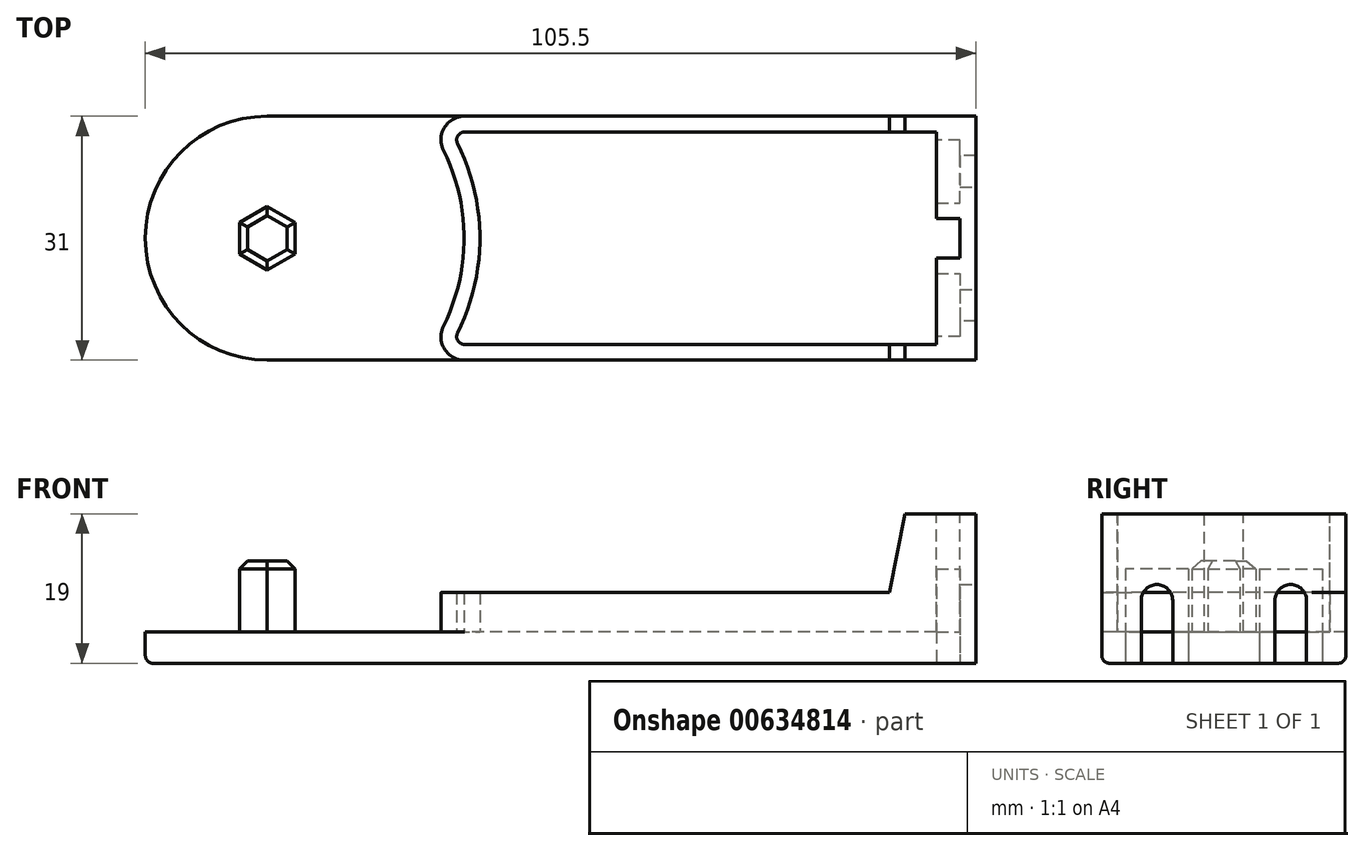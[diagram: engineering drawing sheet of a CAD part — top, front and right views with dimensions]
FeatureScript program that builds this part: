
annotation { "Feature Type Name" : "Feature", "Feature Type Description" : "" }
export const myFeature = defineFeature(function(context is Context, id is Id, definition is map)
    precondition{}
    {
        {
            var Q0;
            Q0=qCreatedBy(makeId("Top.planeOp"),FACE);
            var sketch = newSketch(context, id + "F0", { "sketchPlane" : qUnion([Q0])});
            skCircle(sketch, "E0", {"center": v(0, 0) * mm, "radius": 15.5 * mm});
            skLineSegment(sketch, "E1.bottom", {"start": v(0, 15.5) * mm, "end": v(90, 15.5) * mm});
            skLineSegment(sketch, "E1.top", {"start": v(0, -15.5) * mm, "end": v(90, -15.5) * mm});
            skLineSegment(sketch, "E1.left", {"start": v(0, 15.5) * mm, "end": v(0, -15.5) * mm});
            skLineSegment(sketch, "E1.right", {"start": v(90, 15.5) * mm, "end": v(90, -15.5) * mm});
            skSolve(sketch);
        }
        {
            var Q0;
            Q0=qSketchRegion(id+"F0",true);
            extrude(context, id + "F1", {"entities" : qUnion([Q0]), "depth" : 4 * mm, "offsetDistance" : 25 * mm});
        }
        {
            var Q0;
            Q0=makeQuery(id+"F1.opExtrude","CAP_FACE",FACE,{"disambiguationData":[OSD([sQuery(id+"F0.wireOp",EDGE,"E0"),sQuery(id+"F0.wireOp",EDGE,"E1.bottom"),sQuery(id+"F0.wireOp",EDGE,"E1.top"),sQuery(id+"F0.wireOp",EDGE,"E1.right")])],"isStart":false});
            var sketch = newSketch(context, id + "F2", { "sketchPlane" : qUnion([Q0])});
            skLineSegment(sketch, "E2", {"start": v(0, 0) * mm, "end": v(-3.5, 0) * mm});
            skCircle(sketch, "E3.cCircle", {"center": v(0, 0) * mm, "radius": 3.5 * mm, "construction": true});
            skLineSegment(sketch, "E3.0", {"start": v(-3.5, -2.02) * mm, "end": v(-3.5, 2.02) * mm});
            skLineSegment(sketch, "E3.1", {"start": v(-3.5, 2.02) * mm, "end": v(0, 4.04) * mm});
            skLineSegment(sketch, "E3.2", {"start": v(0, 4.04) * mm, "end": v(3.5, 2.02) * mm});
            skLineSegment(sketch, "E3.3", {"start": v(3.5, 2.02) * mm, "end": v(3.5, -2.02) * mm});
            skLineSegment(sketch, "E3.4", {"start": v(3.5, -2.02) * mm, "end": v(0, -4.04) * mm});
            skLineSegment(sketch, "E3.5", {"start": v(0, -4.04) * mm, "end": v(-3.5, -2.02) * mm});
            skPoint(sketch, "E3.0.midPoint", {"position": v(-3.5, 0) * mm});
            skSolve(sketch);
        }
        {
            var Q0;
            Q0=qSketchRegion(id+"F2",true);
            extrude(context, id + "F3", {"entities" : qUnion([Q0]), "operationType" : NewBodyOperationType.ADD, "depth" : 9 * mm, "offsetDistance" : 25 * mm});
        }
        {
            var Q0;
            Q0=makeQuery(id+"F1.opExtrude","CAP_FACE",FACE,{"disambiguationData":[OSD([sQuery(id+"F0.wireOp",EDGE,"E0"),sQuery(id+"F0.wireOp",EDGE,"E1.bottom"),sQuery(id+"F0.wireOp",EDGE,"E1.top"),sQuery(id+"F0.wireOp",EDGE,"E1.right")])],"isStart":false});
            var sketch = newSketch(context, id + "F4", { "sketchPlane" : qUnion([Q0])});
            skLineSegment(sketch, "E4.top", {"start": v(90, 15.5) * mm, "end": v(25.05, 15.5) * mm});
            skLineSegment(sketch, "E4.left", {"start": v(90, -15.5) * mm, "end": v(90, 15.5) * mm});
            skLineSegment(sketch, "E5.0", {"start": v(88, 13.5) * mm, "end": v(25.05, 13.5) * mm});
            skLineSegment(sketch, "E6.0", {"start": v(88, -13.5) * mm, "end": v(88, 13.5) * mm});
            skArc(sketch, "E7", {"start": v(22.37, -11.16) * mm, "mid": v(25, 0) * mm, "end": v(22.37, 11.16) * mm});
            skArc(sketch, "E8", {"start": v(24.16, -12.05) * mm, "mid": v(27, 0) * mm, "end": v(24.16, 12.05) * mm});
            skLineSegment(sketch, "E9", {"start": v(90, -15.5) * mm, "end": v(25.05, -15.5) * mm});
            skLineSegment(sketch, "E10", {"start": v(25.05, -13.5) * mm, "end": v(88, -13.5) * mm});
            skPoint(sketch, "E11.visualSharp", {"position": v(19.62, -15.5) * mm});
            skArc(sketch, "E11.filletArc", {"start": v(22.37, -11.16) * mm, "mid": v(22.5, -14.08) * mm, "end": v(25.05, -15.5) * mm});
            skPoint(sketch, "E12.visualSharp", {"position": v(23.38, -13.5) * mm});
            skArc(sketch, "E12.filletArc", {"start": v(24.16, -12.05) * mm, "mid": v(24.2, -13.03) * mm, "end": v(25.05, -13.5) * mm});
            skPoint(sketch, "E13.visualSharp", {"position": v(19.62, 15.5) * mm});
            skArc(sketch, "E13.filletArc", {"start": v(25.05, 15.5) * mm, "mid": v(22.5, 14.08) * mm, "end": v(22.37, 11.16) * mm});
            skPoint(sketch, "E14.visualSharp", {"position": v(23.38, 13.5) * mm});
            skArc(sketch, "E14.filletArc", {"start": v(25.05, 13.5) * mm, "mid": v(24.2, 13.03) * mm, "end": v(24.16, 12.05) * mm});
            skSolve(sketch);
        }
        {
            var Q0;
            Q0=qSketchRegion(id+"F4",true);
            extrude(context, id + "F5", {"entities" : qUnion([Q0]), "operationType" : NewBodyOperationType.ADD, "depth" : 15 * mm, "offsetDistance" : 25 * mm});
        }
        {
            var Q0;
            Q0=makeQuery(id+"F5.boolean.opBoolean","MERGE",FACE,{"derivedFrom":[makeQuery(id+"F1.opExtrude","SWEPT_FACE",FACE,{"disambiguationData":[OSD([sQuery(id+"F0.wireOp",EDGE,"E1.top")])]}),makeQuery(id+"F5.opExtrude","SWEPT_FACE",FACE,{"disambiguationData":[OSD([sQuery(id+"F4.wireOp",EDGE,"E4.bottom")])]})]});
            var sketch = newSketch(context, id + "F6", { "sketchPlane" : qUnion([Q0])});
            skLineSegment(sketch, "E15", {"start": v(79, 9) * mm, "end": v(81, 19) * mm});
            skLineSegment(sketch, "E16", {"start": v(20.05, 9) * mm, "end": v(20.05, 19) * mm});
            skLineSegment(sketch, "E17", {"start": v(81, 19) * mm, "end": v(20.05, 19) * mm});
            skLineSegment(sketch, "E18", {"start": v(20.05, 9) * mm, "end": v(79, 9) * mm});
            skSolve(sketch);
        }
        {
            var Q0;
            Q0=qSketchRegion(id+"F6",true);
            extrude(context, id + "F7", {"entities" : qUnion([Q0]), "operationType" : NewBodyOperationType.REMOVE, "oppositeDirection" : true, "depth" : 31 * mm, "offsetDistance" : 25 * mm});
        }
        {
            var Q0;
            Q0=makeQuery(id+"F1.opExtrude","CAP_FACE",FACE,{"disambiguationData":[OSD([sQuery(id+"F0.wireOp",EDGE,"E0"),sQuery(id+"F0.wireOp",EDGE,"E1.bottom"),sQuery(id+"F0.wireOp",EDGE,"E1.top"),sQuery(id+"F0.wireOp",EDGE,"E1.right")])],"isStart":true});
            var sketch = newSketch(context, id + "F8", { "sketchPlane" : qUnion([Q0])});
            skLineSegment(sketch, "E19.bottom", {"start": v(90, 15.5) * mm, "end": v(85, 15.5) * mm});
            skLineSegment(sketch, "E19.top", {"start": v(90, 2.5) * mm, "end": v(85, 2.5) * mm});
            skLineSegment(sketch, "E19.left", {"start": v(90, 15.5) * mm, "end": v(90, 2.5) * mm});
            skLineSegment(sketch, "E19.right", {"start": v(85, 15.5) * mm, "end": v(85, 2.5) * mm});
            skLineSegment(sketch, "E20.bottom", {"start": v(90, -15.5) * mm, "end": v(85, -15.5) * mm});
            skLineSegment(sketch, "E20.top", {"start": v(90, -2.5) * mm, "end": v(85, -2.5) * mm});
            skLineSegment(sketch, "E20.left", {"start": v(90, -15.5) * mm, "end": v(90, -2.5) * mm});
            skLineSegment(sketch, "E20.right", {"start": v(85, -15.5) * mm, "end": v(85, -2.5) * mm});
            skSolve(sketch);
        }
        {
            var Q0;
            Q0=qSketchRegion(id+"F8",true);
            extrude(context, id + "F9", {"entities" : qUnion([Q0]), "operationType" : NewBodyOperationType.ADD, "oppositeDirection" : true, "depth" : 19 * mm, "offsetDistance" : 25 * mm});
        }
        {
            var Q0;
            Q0=makeQuery(id+"F1.opExtrude","CAP_FACE",FACE,{"disambiguationData":[OSD([sQuery(id+"F0.wireOp",EDGE,"E0"),sQuery(id+"F0.wireOp",EDGE,"E1.bottom"),sQuery(id+"F0.wireOp",EDGE,"E1.top"),sQuery(id+"F0.wireOp",EDGE,"E1.right")])],"isStart":true});
            var sketch = newSketch(context, id + "F10", { "sketchPlane" : qUnion([Q0])});
            skLineSegment(sketch, "E21", {"start": v(90, -15.5) * mm, "end": v(90, -10.5) * mm});
            skLineSegment(sketch, "E22", {"start": v(90, -10.5) * mm, "end": v(88, -10.5) * mm});
            skLineSegment(sketch, "E23", {"start": v(88, -10.5) * mm, "end": v(88, -12.5) * mm});
            skLineSegment(sketch, "E24", {"start": v(88, -12.5) * mm, "end": v(85, -12.5) * mm});
            skLineSegment(sketch, "E25", {"start": v(85, -12.5) * mm, "end": v(85, -4.5) * mm});
            skLineSegment(sketch, "E26", {"start": v(85, -4.5) * mm, "end": v(88, -4.5) * mm});
            skLineSegment(sketch, "E27", {"start": v(88, -4.5) * mm, "end": v(88, -6.5) * mm});
            skLineSegment(sketch, "E28", {"start": v(88, -6.5) * mm, "end": v(90, -6.5) * mm});
            skLineSegment(sketch, "E29", {"start": v(90, -6.5) * mm, "end": v(90, -10.5) * mm});
            skLineSegment(sketch, "E30", {"start": v(0, 0) * mm, "end": v(90, 0) * mm, "construction": true});
            skLineSegment(sketch, "E31.MirrorCS", {"start": v(90, 6.5) * mm, "end": v(90, 10.5) * mm});
            skLineSegment(sketch, "E32.MirrorCS", {"start": v(88, 6.5) * mm, "end": v(90, 6.5) * mm});
            skLineSegment(sketch, "E33.MirrorCS", {"start": v(90, 15.5) * mm, "end": v(90, 10.5) * mm});
            skLineSegment(sketch, "E34.MirrorCS", {"start": v(88, 4.5) * mm, "end": v(88, 6.5) * mm});
            skLineSegment(sketch, "E35.MirrorCS", {"start": v(90, 10.5) * mm, "end": v(88, 10.5) * mm});
            skLineSegment(sketch, "E36.MirrorCS", {"start": v(88, 12.5) * mm, "end": v(85, 12.5) * mm});
            skLineSegment(sketch, "E37.MirrorCS", {"start": v(88, 10.5) * mm, "end": v(88, 12.5) * mm});
            skLineSegment(sketch, "E38.MirrorCS", {"start": v(85, 4.5) * mm, "end": v(88, 4.5) * mm});
            skLineSegment(sketch, "E39.MirrorCS", {"start": v(85, 12.5) * mm, "end": v(85, 4.5) * mm});
            skSolve(sketch);
        }
        {
            var Q0;
            Q0=qSketchRegion(id+"F10",true);
            extrude(context, id + "F11", {"entities" : qUnion([Q0]), "operationType" : NewBodyOperationType.REMOVE, "oppositeDirection" : true, "depth" : 12 * mm, "offsetDistance" : 25 * mm});
        }
        {
            var Q0;
            Q0=makeQuery(id+"F5.boolean.opBoolean","MERGE",FACE,{"derivedFrom":[makeQuery(id+"F1.opExtrude","SWEPT_FACE",FACE,{"disambiguationData":[OSD([sQuery(id+"F0.wireOp",EDGE,"E1.right")])]}),makeQuery(id+"F5.opExtrude","SWEPT_FACE",FACE,{"disambiguationData":[OSD([sQuery(id+"F4.wireOp",EDGE,"E4.left")])]})]});
            var sketch = newSketch(context, id + "F12", { "sketchPlane" : qUnion([Q0])});
            skLineSegment(sketch, "E40.bottom", {"start": v(10.5, 12) * mm, "end": v(6.5, 12) * mm});
            skLineSegment(sketch, "E40.left", {"start": v(10.5, 12) * mm, "end": v(10.5, 8) * mm});
            skLineSegment(sketch, "E40.right", {"start": v(6.5, 12) * mm, "end": v(6.5, 8) * mm});
            skLineSegment(sketch, "E41.bottom", {"start": v(-6.5, 12) * mm, "end": v(-10.5, 12) * mm});
            skLineSegment(sketch, "E41.left", {"start": v(-6.5, 12) * mm, "end": v(-6.5, 8) * mm});
            skLineSegment(sketch, "E41.right", {"start": v(-10.5, 12) * mm, "end": v(-10.5, 8) * mm});
            skArc(sketch, "E42", {"start": v(10.5, 8) * mm, "mid": v(8.5, 10) * mm, "end": v(6.5, 8) * mm});
            skArc(sketch, "E43", {"start": v(-6.5, 8) * mm, "mid": v(-8.5, 10) * mm, "end": v(-10.5, 8) * mm});
            skSolve(sketch);
        }
        {
            var Q0;
            Q0=qSketchRegion(id+"F12",true);
            extrude(context, id + "F13", {"entities" : qUnion([Q0]), "operationType" : NewBodyOperationType.ADD, "oppositeDirection" : true, "depth" : 2 * mm, "offsetDistance" : 25 * mm});
        }
        {
            var Q0;
            Q0=makeQuery(id+"F1.opExtrude","CAP_EDGE",EDGE,{"disambiguationData":[OSD([sQuery(id+"F0.wireOp",EDGE,"E1.top")])],"isStart":true});
            fillet(context, id + "F14", {"entities" : qUnion([Q0]), "radius" : 1 * mm, "tangentPropagation" : true, "allowEdgeOverflow" : false});
        }
        {
            var Q0;
            Q0=makeQuery(id+"F3.opExtrude","CAP_EDGE",EDGE,{"disambiguationData":[OSD([sQuery(id+"F2.wireOp",EDGE,"E3.5")])],"isStart":false});
            var Q1;
            Q1=makeQuery(id+"F3.opExtrude","CAP_EDGE",EDGE,{"disambiguationData":[OSD([sQuery(id+"F2.wireOp",EDGE,"E3.4")])],"isStart":false});
            var Q2;
            Q2=makeQuery(id+"F3.opExtrude","CAP_EDGE",EDGE,{"disambiguationData":[OSD([sQuery(id+"F2.wireOp",EDGE,"E3.3")])],"isStart":false});
            var Q3;
            Q3=makeQuery(id+"F3.opExtrude","CAP_EDGE",EDGE,{"disambiguationData":[OSD([sQuery(id+"F2.wireOp",EDGE,"E3.2")])],"isStart":false});
            var Q4;
            Q4=makeQuery(id+"F3.opExtrude","CAP_EDGE",EDGE,{"disambiguationData":[OSD([sQuery(id+"F2.wireOp",EDGE,"E3.1")])],"isStart":false});
            var Q5;
            Q5=makeQuery(id+"F3.opExtrude","CAP_EDGE",EDGE,{"disambiguationData":[OSD([sQuery(id+"F2.wireOp",EDGE,"E3.0")])],"isStart":false});
            chamfer(context, id + "F15", {"entities" : qUnion([Q0, Q1, Q2, Q3, Q4, Q5]), "width" : 1 * mm, "tangentPropagation" : true});
        }
    });
